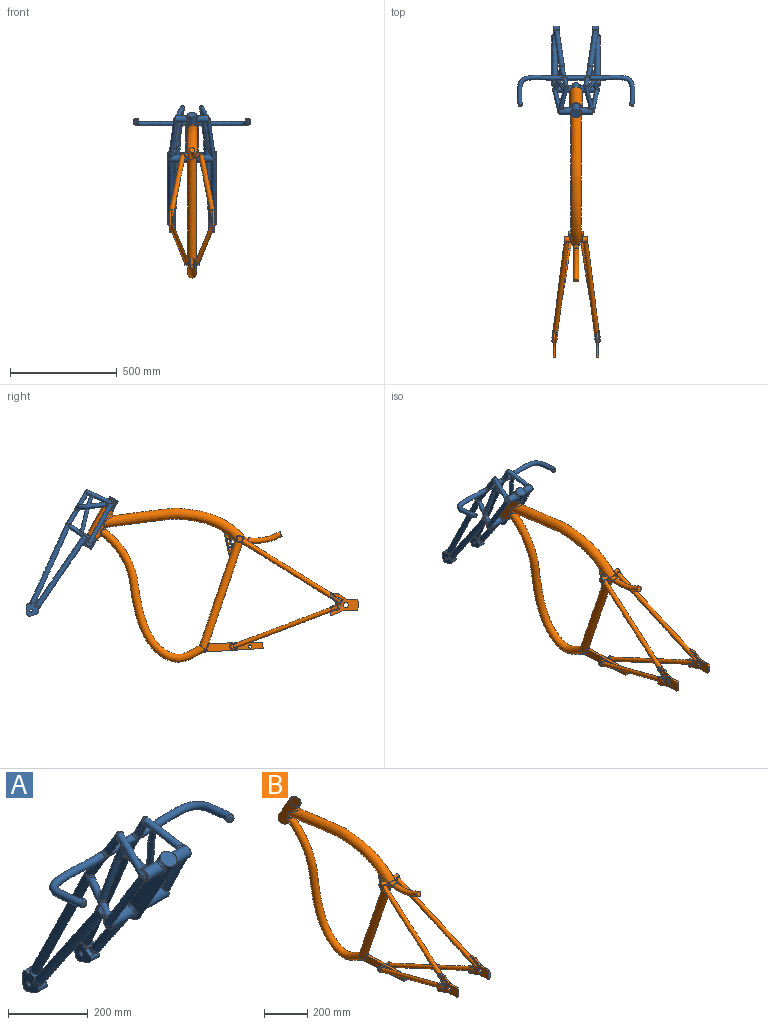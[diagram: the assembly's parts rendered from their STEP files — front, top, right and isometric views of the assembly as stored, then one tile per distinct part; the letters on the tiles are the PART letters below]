
ASSEMBLY  parts=2 mates=1
PART A: 124 faces, bbox 553.6x434.4x597.8 mm
  f0: plane 24.39x8.77mm, normal (0.09,0.58,-0.81), area 177mm2, adj f52,f55
  f1: cylinder r=12.5mm len=27.12mm, axis (-0.09,-0.58,0.81), area 754.7mm2, adj f48,f49,f50,f51,f57,f110,f111,f112
  f2: cylinder r=12.5mm len=27.12mm, axis (0.09,-0.58,0.81), area 754.7mm2, adj f35,f58,f59,f60,f63,f104,f105,f106
  f3: cylinder r=12.5mm len=25.53mm, axis (0.09,-0.58,0.81), area 364mm2, adj f61,f62,f63,f65,f101,f103
  f4: bspline ~89.4x61.57mm, area 4951.9mm2, adj f66,f90,f121,f122
  f5: bspline ~81.91x57.27mm, area 4325.2mm2, adj f79,f89,f120
  f6: bspline ~89.4x61.57mm, area 4951.7mm2, adj f56,f67,f114,f115
  f7: bspline ~81.91x57.27mm, area 4325.3mm2, adj f68,f70,f119
  f8: plane 3.04x1.93mm, normal (-0.24,-0.86,-0.46), area 3.5mm2, adj f30,f84,f88
  f9: plane 4.38x2.58mm, normal (0.24,-0.86,-0.46), area 1mm2, adj f39,f43
  f10: bspline ~109.3x81.16mm, area 5787.7mm2, adj f15,f23,f31,f35,f65,f66,f81,f90
  f11: cylinder r=16.33mm len=61.66mm, axis (1,0,0), area 4732.4mm2, adj f19,f39,f71,f76,f77,f94
  f12: plane 3.65x3.13mm, normal (1,0,0), area 1.5mm2, adj f39,f43,f77
  f13: cylinder r=16.33mm len=82.32mm, axis (1,0,0), area 7483.8mm2, adj f22,f36,f39,f40,f44,f92
  f14: plane 29.1x20.74mm, normal (-1,0,0), area 95.1mm2, adj f20,f82,f85,f86,f88
  f15: cylinder r=16.33mm len=82.32mm, axis (1,0,0), area 7485.1mm2, adj f10,f23,f26,f27,f31,f91
  f16: cylinder r=22.49mm len=247.36mm, axis (0,0.49,-0.87), area 30990.3mm2, adj f17,f18,f91,f92,f93,f94
  f17: plane 44.97x39.31mm, normal (0,-0.49,0.87), area 1588.4mm2, adj f16
  f18: plane 44.97x39.31mm, normal (0,0.49,-0.87), area 1588.4mm2, adj f16
  f19: plane 29.1x20.74mm, normal (1,0,0), area 95.1mm2, adj f11,f71,f72,f75,f76
  f20: cylinder r=16.33mm len=61.66mm, axis (1,0,0), area 4735.2mm2, adj f14,f26,f82,f83,f86,f93
  f21: plane 3.65x3.12mm, normal (-1,0,0), area 1.5mm2, adj f26,f30,f83
  f22: plane 32.69x28.52mm, normal (1,0,0), area 505.8mm2, adj f13,f36,f38,f39,f44
  f23: plane 32.69x28.52mm, normal (-1,0,0), area 505.8mm2, adj f10,f15,f25,f26,f31
  f24: plane 1.65x1.36mm, normal (0,-0.49,0.87), area 1mm2, adj f26,f84,f85
  f25: plane 17.48x10mm, normal (0,0.49,-0.87), area 157.1mm2, adj f23,f26
  f26: bspline ~197.67x121.81mm, area 12140mm2, adj f15,f20,f21,f23,f24,f25,f27,f28
  f27: plane 1.86x1.53mm, normal (-0.25,-0.76,-0.59), area 1.6mm2, adj f15,f26,f31
  f28: plane 4.38x2.58mm, normal (-0.24,-0.86,-0.46), area 1mm2, adj f26,f30
  f29: plane 11.6x8.61mm, normal (-0.25,-0.76,-0.59), area 27mm2, adj f26,f31
  f30: bspline ~130.96x72.65mm, area 6497mm2, adj f8,f21,f26,f28,f79,f80,f83,f84
  f31: bspline ~20.64x17.61mm, area 152.1mm2, adj f10,f15,f23,f26,f27,f29
  f32: bspline ~84.78x49.1mm, area 2363mm2, adj f33,f80
  f33: bspline ~140.91x45.51mm, area 6912.3mm2, adj f32,f81
  f34: plane 21.62x15.63mm, normal (0.09,-0.58,0.81), area 126.5mm2, adj f35,f118
  f35: bspline ~341.51x244.41mm, area 30533.3mm2, adj f2,f10,f34,f118
  f36: bspline ~109.3x81.16mm, area 5787.7mm2, adj f13,f22,f44,f48,f54,f56,f67,f78
  f37: plane 1.65x1.36mm, normal (0,-0.49,0.87), area 1mm2, adj f39,f72,f73
  f38: plane 17.48x10mm, normal (0,0.49,-0.87), area 157.1mm2, adj f22,f39
  f39: bspline ~197.67x121.81mm, area 12140mm2, adj f9,f11,f12,f13,f22,f37,f38,f40
  f40: plane 1.86x1.53mm, normal (0.25,-0.76,-0.59), area 1.6mm2, adj f13,f39,f44
  f41: plane 3.04x1.93mm, normal (0.24,-0.86,-0.46), area 3.5mm2, adj f43,f73,f75
  f42: plane 11.6x8.61mm, normal (0.25,-0.76,-0.59), area 27mm2, adj f39,f44
  f43: bspline ~130.96x72.65mm, area 6497mm2, adj f9,f12,f39,f41,f68,f69,f70,f73
  f44: bspline ~20.64x17.61mm, area 152.1mm2, adj f13,f22,f36,f39,f40,f42
  f45: bspline ~84.78x49.1mm, area 2363mm2, adj f46,f69
  f46: bspline ~140.91x45.51mm, area 6912.3mm2, adj f45,f78
  f47: plane 21.62x15.63mm, normal (-0.09,-0.58,0.81), area 126.5mm2, adj f48,f116
  f48: bspline ~341.51x244.41mm, area 30533.3mm2, adj f1,f36,f47,f116
  f49: extruded ~50.08x36.73mm, area 2051.5mm2, adj f1,f50,f52,f57,f110,f113
  f50: plane 65.89x61.72mm, normal (1,0,0), area 2550.6mm2, adj f1,f49,f51,f52,f53,f57
  f51: plane 29.55x17.87mm, normal (0,-0.52,0.85), area 212.1mm2, adj f1,f50,f52,f54,f55,f109,f112,f113
  f52: extruded ~61.93x29mm, area 2324.9mm2, adj f0,f49,f50,f51,f55,f108,f113
  f53: cylinder r=6.55mm len=29mm, axis (-1,0,0), area 1192.9mm2, adj f50,f113
  f54: bspline ~378.92x185.95mm, area 31091.1mm2, adj f36,f51,f55,f56,f107,f109
  f55: cylinder r=12.5mm len=25.53mm, axis (-0.09,-0.58,0.81), area 364mm2, adj f0,f51,f52,f54,f107,f108
  f56: plane 24.9x17.76mm, normal (-0.09,-0.58,0.81), area 113.5mm2, adj f6,f36,f54
  f57: plane 20.36x18.65mm, normal (0.09,0.58,-0.81), area 128.3mm2, adj f1,f49,f50
  f58: plane 20.36x18.65mm, normal (-0.09,0.58,-0.81), area 128.3mm2, adj f2,f59,f60
  f59: extruded ~50.08x36.73mm, area 2051.5mm2, adj f2,f58,f60,f62,f100,f106
  f60: plane 65.89x61.72mm, normal (-1,0,0), area 2550.6mm2, adj f2,f58,f59,f62,f63,f64
  f61: plane 24.39x8.77mm, normal (-0.09,0.58,-0.81), area 177mm2, adj f3,f62
  f62: extruded ~61.93x29mm, area 2324.9mm2, adj f3,f59,f60,f61,f63,f100,f101
  f63: plane 29.55x17.87mm, normal (0,-0.52,0.85), area 212.1mm2, adj f2,f3,f60,f62,f65,f100,f102,f105
  f64: cylinder r=6.55mm len=29mm, axis (1,0,0), area 1192.9mm2, adj f60,f100
  f65: bspline ~378.92x185.95mm, area 31091.1mm2, adj f3,f10,f63,f66,f102,f103
  f66: plane 24.9x17.76mm, normal (0.09,-0.58,0.81), area 113.5mm2, adj f4,f10,f65
  f67: bspline ~19.67x18.98mm, area 0mm2, adj f6,f36
  f68: bspline ~19.98x15.01mm, area 0mm2, adj f7,f43
  f69: bspline ~25.71x19.37mm, area 412.7mm2, adj f43,f45,f70
  f70: bspline ~20.39x19.79mm, area 187.8mm2, adj f7,f43,f69
  f71: bspline ~40.11x24.27mm, area 94.2mm2, adj f11,f19,f39,f72
  f72: cylinder r=6mm len=9.6mm, axis (0,-0.87,-0.49), area 39.6mm2, adj f19,f37,f39,f71,f74
  f73: cylinder r=6mm len=8.58mm, axis (-0.97,-0.21,-0.12), area 37.4mm2, adj f37,f39,f41,f43,f74
  f74: sphere r=6mm, area 47.4mm2, adj f72,f73,f75
  f75: cylinder r=6mm len=10.5mm, axis (0,0.47,-0.88), area 38.8mm2, adj f19,f41,f43,f74,f76
  f76: bspline ~35.25x16.64mm, area 131.8mm2, adj f11,f19,f43,f75,f77
  f77: bspline ~28.35x22.14mm, area 351mm2, adj f11,f12,f39,f43,f76
  f78: bspline ~25.05x23.15mm, area 437.1mm2, adj f36,f46
  f79: bspline ~20.39x19.79mm, area 187.8mm2, adj f5,f30,f80
  f80: bspline ~25.71x19.38mm, area 412.8mm2, adj f30,f32,f79
  f81: bspline ~25.05x23.15mm, area 437.1mm2, adj f10,f33
  f82: bspline ~37.76x23.12mm, area 94.1mm2, adj f14,f20,f26,f85
  f83: bspline ~28.35x22.14mm, area 351mm2, adj f20,f21,f26,f30,f86
  f84: cylinder r=6mm len=8.58mm, axis (0.97,-0.21,-0.12), area 37.4mm2, adj f8,f24,f26,f30,f87
  f85: cylinder r=6mm len=9.6mm, axis (0,0.87,0.49), area 39.6mm2, adj f14,f24,f26,f82,f87
  f86: bspline ~35.25x16.64mm, area 131.8mm2, adj f14,f20,f30,f83,f88
  f87: sphere r=6mm, area 35.8mm2, adj f84,f85,f88
  f88: cylinder r=6mm len=10.5mm, axis (0,-0.47,0.88), area 38.8mm2, adj f8,f14,f30,f86,f87
  f89: bspline ~19.98x15.01mm, area 0mm2, adj f5,f30
  f90: bspline ~19.67x18.98mm, area 0mm2, adj f4,f10
  f91: bspline ~42.66x37.71mm, area 790.4mm2, adj f15,f16
  f92: bspline ~42.64x37.7mm, area 790.6mm2, adj f13,f16
  f93: bspline ~42.66x37.71mm, area 790.3mm2, adj f16,f20
  f94: bspline ~42.66x37.7mm, area 790.9mm2, adj f11,f16
  f95: cylinder r=10.69mm len=138mm, axis (1,0,0), area 6988.7mm2, adj f97,f99,f114,f119,f120,f121
  f96: plane 11.33x10.58mm, normal (-0.36,-0.93,0.1), area 101.3mm2, adj f117
  f97: bspline ~206.22x143.31mm, area 20389.5mm2, adj f95,f115,f117
  f98: plane 11.34x10.59mm, normal (0.36,-0.93,0.1), area 101.3mm2, adj f123
  f99: bspline ~206.22x143.31mm, area 20389.5mm2, adj f95,f122,f123
  f100: plane 61.61x61.26mm, normal (1,0,0), area 2422mm2, adj f59,f62,f63,f64,f101,f102,f103,f104
  f101: plane 12.86x11.39mm, normal (0,-0.58,0.82), area 37.2mm2, adj f3,f62,f100,f103
  f102: extruded ~9.97x0.72mm, area 7.9mm2, adj f63,f65,f100,f103
  f103: extruded ~10.8x5.8mm, area 71.6mm2, adj f3,f65,f100,f101,f102
  f104: plane 15.67x15mm, normal (0,-0.58,0.82), area 227.8mm2, adj f2,f100,f105,f106
  f105: extruded ~15x9.08mm, area 159.8mm2, adj f2,f63,f100,f104
  f106: extruded ~15x0.62mm, area 12mm2, adj f2,f59,f100,f104
  f107: extruded ~10.8x5.8mm, area 71.6mm2, adj f54,f55,f108,f109,f113
  f108: plane 12.86x11.39mm, normal (0,-0.58,0.82), area 37.2mm2, adj f52,f55,f107,f113
  f109: extruded ~9.97x0.72mm, area 7.9mm2, adj f51,f54,f107,f113
  f110: extruded ~15x0.62mm, area 12mm2, adj f1,f49,f111,f113
  f111: plane 15.67x15mm, normal (0,-0.58,0.82), area 227.8mm2, adj f1,f110,f112,f113
  f112: extruded ~15x9.08mm, area 159.8mm2, adj f1,f51,f111,f113
  f113: plane 61.61x61.26mm, normal (-1,0,0), area 2422mm2, adj f49,f51,f52,f53,f107,f108,f109,f110
  f114: bspline ~27.27x19.55mm, area 281.1mm2, adj f6,f95,f115
  f115: bspline ~12.4x10.19mm, area 66.2mm2, adj f6,f97,f114
  f116: cylinder r=5mm len=22.71mm, axis (-0.25,0.8,0.54), area 147.6mm2, adj f36,f47,f48
  f117: bspline ~21.88x21.78mm, area 437.6mm2, adj f96,f97
  f118: cylinder r=5mm len=22.71mm, axis (0.25,0.8,0.54), area 147.6mm2, adj f10,f34,f35
  f119: bspline ~30.21x19.28mm, area 374.4mm2, adj f7,f95
  f120: bspline ~30.22x19.28mm, area 374.3mm2, adj f5,f95
  f121: bspline ~27.26x19.55mm, area 280.8mm2, adj f4,f95,f122
  f122: bspline ~12.5x10.39mm, area 66.2mm2, adj f4,f99,f121
  f123: bspline ~21.9x21.79mm, area 437.6mm2, adj f98,f99
PART B: 192 faces, bbox 230.8x1270.5x735.8 mm
  f0: bspline ~21.42x11.61mm, area 143.6mm2, adj f27,f165,f167,f168
  f1: bspline ~17.59x9.63mm, area 44.3mm2, adj f27,f164,f166,f171
  f2: bspline ~17.9x15.68mm, area 126mm2, adj f24,f171,f180,f184
  f3: bspline ~17.06x12.17mm, area 42.7mm2, adj f24,f167,f172,f173
  f4: plane 3.6x3.57mm, normal (-1,0,0), area 5.2mm2, adj f167,f174,f175
  f5: plane 28.04x21.48mm, normal (-1,0,0), area 263.4mm2, adj f167,f174,f181,f182
  f6: plane 6.88x5.58mm, normal (-1,0,0), area 14.1mm2, adj f174,f175,f182
  f7: plane 3.6x3.57mm, normal (1,0,0), area 5.2mm2, adj f171,f178,f179
  f8: plane 33.48x16.92mm, normal (1,0,0), area 255mm2, adj f170,f171,f178,f183
  f9: plane 6.88x5.58mm, normal (1,0,0), area 14.1mm2, adj f178,f179,f183
  f10: plane 4.96x2.3mm, normal (0,-0.45,-0.89), area 1.5mm2, adj f43,f151,f157
  f11: plane 132.93x37.64mm, normal (1,0,0), area 3689.4mm2, adj f29,f30,f31,f32,f137
  f12: plane 131.21x42.91mm, normal (-1,0,0), area 3945.4mm2, adj f29,f31,f110,f112,f113,f119
  f13: plane 14.26x5.68mm, normal (0,0.93,-0.35), area 13.8mm2, adj f14,f104,f114,f115
  f14: bspline ~493.81x203.46mm, area 31729.8mm2, adj f13,f15,f83,f101,f102,f114,f115,f116
  f15: plane 12.74x5.39mm, normal (0,1,0), area 9.9mm2, adj f14,f82,f99,f122,f125
  f16: plane 6.18x3.94mm, normal (-0.1,-0.84,-0.53), area 2.6mm2, adj f76,f131
  f17: plane 14.26x5.68mm, normal (0,0.93,-0.35), area 13.8mm2, adj f18,f73,f132,f133
  f18: bspline ~493.81x203.46mm, area 31729.8mm2, adj f17,f19,f64,f71,f72,f132,f133,f135
  f19: plane 14.81x13.34mm, normal (0,1,0), area 85.4mm2, adj f18,f63,f69,f70,f140,f143
  f20: plane 6.18x3.94mm, normal (0.1,-0.84,-0.53), area 2.6mm2, adj f46,f149
  f21: plane 16.94x10.55mm, normal (0,-0.45,-0.89), area 35.5mm2, adj f24,f27,f42,f152,f153
  f22: plane 16.94x10.55mm, normal (0,-0.45,-0.89), area 35.5mm2, adj f24,f27,f43,f150,f151
  f23: bspline ~628.58x495.84mm, area 101545mm2, adj f106,f108,f109,f110,f111,f155,f156
  f24: bspline ~656.99x154.64mm, area 101847.3mm2, adj f2,f3,f21,f22,f27,f151,f153,f154
  f25: plane 0.21x0mm, normal (0,-0.23,0.97), area 0mm2, adj f42,f152,f157
  f26: plane 0.21x0mm, normal (0,-0.23,0.97), area 0mm2, adj f43,f150,f157
  f27: bspline ~545.85x252.61mm, area 60746.3mm2, adj f0,f1,f21,f22,f24,f29,f36,f105
  f28: plane 4.97x2.3mm, normal (0,-0.45,-0.89), area 1.5mm2, adj f42,f153,f157
  f29: plane 256.89x20.13mm, normal (0,0.02,1), area 3223mm2, adj f11,f12,f27,f30,f33,f34,f105,f113
  f30: plane 29.33x12.7mm, normal (0,-1,0.05), area 372.8mm2, adj f11,f29,f31,f34
  f31: plane 279.37x17.58mm, normal (0,-0.06,-1), area 3534.2mm2, adj f11,f12,f30,f33,f34,f108,f109,f110
  f32: cylinder r=7.75mm len=15.51mm, axis (-1,0,0), area 618.8mm2, adj f11,f34
  f33: plane 131.21x42.91mm, normal (1,0,0), area 3945.4mm2, adj f29,f31,f105,f107,f108,f136
  f34: plane 132.93x37.64mm, normal (-1,0,0), area 3689.4mm2, adj f29,f30,f31,f32,f118
  f35: plane 28.93x26.96mm, normal (0,-0.92,0.39), area 506.7mm2, adj f36
  f36: bspline ~184.62x54.91mm, area 13445.3mm2, adj f27,f35,f157
  f37: plane 58.44x51.08mm, normal (0,-0.49,0.87), area 851.6mm2, adj f38,f40
  f38: cylinder r=29.22mm len=161.12mm, axis (0,0.49,-0.87), area 22591mm2, adj f37,f39,f154,f155
  f39: plane 58.44x51.08mm, normal (0,0.49,-0.87), area 851.6mm2, adj f38,f40
  f40: cylinder r=24.14mm len=156.19mm, axis (0,-0.49,0.87), area 23033.3mm2, adj f37,f39
  f41: plane 26.88x26.88mm, normal (1,0,0), area 506.7mm2, adj f42,f191
  f42: cylinder r=12.7mm len=39.18mm, axis (1,0,0), area 1803.5mm2, adj f21,f25,f28,f41,f152,f153,f157,f190
  f43: cylinder r=12.7mm len=39.18mm, axis (1,0,0), area 1802.3mm2, adj f10,f22,f26,f44,f150,f151,f157,f188
  f44: plane 26.88x26.88mm, normal (-1,0,0), area 506.7mm2, adj f43,f189
  f45: plane 12.62x8.29mm, normal (0.1,-0.84,-0.53), area 20.5mm2, adj f46,f47,f146
  f46: bspline ~482.12x311.22mm, area 37814.4mm2, adj f20,f45,f47,f48,f50,f51,f52,f144
  f47: bspline ~492.82x318.16mm, area 208.1mm2, adj f45,f46,f145,f146
  f48: plane 2.59x1.24mm, normal (0,1,0), area 0.5mm2, adj f46,f50,f144
  f49: plane 19.65x15.46mm, normal (0,0.62,-0.79), area 214mm2, adj f50,f68,f69,f147
  f50: cylinder r=12.08mm len=12.54mm, axis (-1,0,0), area 69.4mm2, adj f46,f48,f49,f69,f144,f147
  f51: plane 1.61x0.71mm, normal (0,1,0), area 0.2mm2, adj f46,f52,f145
  f52: plane 37.77x14.13mm, normal (0,0,1), area 240.4mm2, adj f46,f51,f53,f69,f70,f145,f148
  f53: cylinder r=8.03mm len=8.13mm, axis (-1,0,0), area 40.1mm2, adj f52,f54,f69,f70
  f54: plane 30.55x20.87mm, normal (0,-0.56,0.83), area 300.7mm2, adj f53,f55,f69,f70
  f55: cylinder r=11.7mm len=8.13mm, axis (-1,0,0), area 71.8mm2, adj f54,f56,f69,f70
  f56: plane 46.43x8.13mm, normal (0,0,1), area 377.4mm2, adj f55,f57,f69,f70
  f57: plane 10.86x8.13mm, normal (0,-0.92,0.38), area 95.5mm2, adj f56,f58,f69,f70
  f58: plane 29.49x8.13mm, normal (0,-1,0), area 239.7mm2, adj f57,f59,f69,f70
  f59: plane 10.5x8.13mm, normal (0,-0.93,-0.36), area 91.5mm2, adj f58,f60,f69,f70
  f60: plane 46.87x8.13mm, normal (0,0,-1), area 380.9mm2, adj f59,f61,f69,f70
  f61: cylinder r=47.47mm len=14.09mm, axis (-1,0,0), area 116.3mm2, adj f60,f62,f69,f70
  f62: plane 56.04x21.17mm, normal (0,-0.35,-0.94), area 486.9mm2, adj f61,f63,f69,f70
  f63: cylinder r=6.32mm len=9.34mm, axis (-1,0,0), area 106.3mm2, adj f19,f62,f69,f70
  f64: plane 12.76x5.41mm, normal (0,1,0), area 9.9mm2, adj f18,f65,f69,f139,f142
  f65: cylinder r=6.14mm len=10.18mm, axis (-1,0,0), area 89.1mm2, adj f64,f66,f69,f142
  f66: plane 17.56x8.16mm, normal (0,0.38,0.93), area 153.9mm2, adj f65,f68,f69,f70,f142
  f67: cylinder r=12.06mm len=24.13mm, axis (-1,0,0), area 616.1mm2, adj f69,f70
  f68: cylinder r=6.18mm len=11.22mm, axis (-1,0,0), area 114.4mm2, adj f49,f66,f69,f70,f147
  f69: plane 130.4x100.38mm, normal (1,0,0), area 5367.7mm2, adj f19,f49,f50,f52,f53,f54,f55,f56
  f70: plane 130.4x100.38mm, normal (-1,0,0), area 5021.1mm2, adj f19,f52,f53,f54,f55,f56,f57,f58
  f71: plane 22.2x9.07mm, normal (0,-0.93,0.35), area 56.7mm2, adj f18,f70,f142,f143
  f72: plane 11x4.62mm, normal (0,-0.93,0.35), area 12mm2, adj f18,f141
  f73: plane 24.79x23.39mm, normal (1,0,0), area 289.5mm2, adj f17,f74,f132,f133,f135
  f74: cylinder r=12.39mm len=24.77mm, axis (1,0,0), area 1159.1mm2, adj f73,f134,f135,f136,f137,f138
  f75: plane 12.62x8.29mm, normal (-0.1,-0.84,-0.53), area 20.5mm2, adj f76,f77,f128
  f76: bspline ~482.12x311.22mm, area 37814.3mm2, adj f16,f75,f77,f78,f95,f96,f98,f127
  f77: bspline ~492.82x318.16mm, area 208.1mm2, adj f75,f76,f126,f128
  f78: plane 2.59x1.24mm, normal (0,1,0), area 0.5mm2, adj f76,f98,f127
  f79: plane 19.65x15.46mm, normal (0,0.62,-0.79), area 214mm2, adj f80,f98,f99,f130
  f80: cylinder r=6.18mm len=11.22mm, axis (1,0,0), area 114.4mm2, adj f79,f81,f99,f100,f130
  f81: plane 17.56x8.15mm, normal (0,0.38,0.93), area 153.9mm2, adj f80,f82,f99,f100,f125
  f82: cylinder r=6.14mm len=10.18mm, axis (1,0,0), area 89.1mm2, adj f15,f81,f99,f125
  f83: plane 14.82x13.35mm, normal (0,1,0), area 85.4mm2, adj f14,f84,f99,f100,f121,f124
  f84: cylinder r=6.32mm len=9.34mm, axis (1,0,0), area 106.3mm2, adj f83,f85,f99,f100
  f85: plane 56.04x21.17mm, normal (0,-0.35,-0.94), area 486.9mm2, adj f84,f86,f99,f100
  f86: cylinder r=47.47mm len=14.09mm, axis (1,0,0), area 116.3mm2, adj f85,f87,f99,f100
  f87: plane 46.87x8.13mm, normal (0,0,-1), area 380.9mm2, adj f86,f88,f99,f100
  f88: plane 10.5x8.13mm, normal (0,-0.93,-0.36), area 91.5mm2, adj f87,f89,f99,f100
  f89: plane 29.49x8.13mm, normal (0,-1,0), area 239.7mm2, adj f88,f90,f99,f100
  f90: plane 10.86x8.13mm, normal (0,-0.92,0.38), area 95.5mm2, adj f89,f91,f99,f100
  f91: plane 46.43x8.13mm, normal (0,0,1), area 377.4mm2, adj f90,f92,f99,f100
  f92: cylinder r=11.7mm len=8.13mm, axis (1,0,0), area 71.8mm2, adj f91,f93,f99,f100
  f93: plane 30.55x20.87mm, normal (0,-0.56,0.83), area 300.7mm2, adj f92,f94,f99,f100
  f94: cylinder r=8.03mm len=8.13mm, axis (1,0,0), area 40.1mm2, adj f93,f95,f99,f100
  f95: plane 37.73x14.09mm, normal (0,0,1), area 240.4mm2, adj f76,f94,f96,f99,f100,f126,f129
  f96: plane 1.61x0.71mm, normal (0,1,0), area 0.2mm2, adj f76,f95,f126
  f97: cylinder r=12.06mm len=24.13mm, axis (1,0,0), area 616.1mm2, adj f99,f100
  f98: cylinder r=12.08mm len=12.54mm, axis (1,0,0), area 69.4mm2, adj f76,f78,f79,f99,f127,f130
  f99: plane 130.4x100.38mm, normal (-1,0,0), area 5367.7mm2, adj f15,f79,f80,f81,f82,f83,f84,f85
  f100: plane 130.4x100.38mm, normal (1,0,0), area 5021.1mm2, adj f80,f81,f83,f84,f85,f86,f87,f88
  f101: plane 22.2x9.07mm, normal (0,-0.93,0.35), area 56.7mm2, adj f14,f100,f124,f125
  f102: plane 11x4.62mm, normal (0,-0.93,0.35), area 12mm2, adj f14,f123
  f103: cylinder r=12.39mm len=24.77mm, axis (-1,0,0), area 1159.1mm2, adj f104,f116,f117,f118,f119,f120
  f104: plane 24.8x23.39mm, normal (-1,0,0), area 289.5mm2, adj f13,f103,f114,f115,f116
  f105: cylinder r=6mm len=33.44mm, axis (0,-0.32,0.95), area 206.6mm2, adj f27,f29,f33,f107
  f106: bspline ~14.59x12.57mm, area 28.3mm2, adj f23,f27,f107
  f107: bspline ~9.22x8.89mm, area 34.9mm2, adj f33,f105,f106,f108
  f108: bspline ~31.49x21.1mm, area 78.1mm2, adj f23,f31,f33,f107,f109
  f109: bspline ~26.84x11.09mm, area 62.9mm2, adj f23,f31,f108,f110
  f110: bspline ~31.49x21.1mm, area 78.1mm2, adj f12,f23,f31,f109,f112
  f111: bspline ~14.96x12.88mm, area 28.3mm2, adj f23,f27,f112
  f112: bspline ~9.3x8.79mm, area 34.9mm2, adj f12,f110,f111,f113
  f113: cylinder r=6mm len=33.44mm, axis (0,-0.32,0.95), area 206.6mm2, adj f12,f27,f29,f112
  f114: bspline ~19.77x6.98mm, area 43mm2, adj f13,f14,f104,f116
  f115: bspline ~18.25x12.67mm, area 43mm2, adj f13,f14,f104,f116
  f116: bspline ~29.05x20.81mm, area 285.2mm2, adj f14,f103,f104,f114,f115,f118
  f117: bspline ~17.39x6.72mm, area 100.7mm2, adj f29,f103,f118,f119
  f118: torus R=18.39mm, axis (1,0,0), area 334.7mm2, adj f34,f103,f116,f117,f120
  f119: torus R=18.39mm, axis (1,0,0), area 348mm2, adj f12,f103,f117,f120
  f120: bspline ~7.83x6.26mm, area 56.8mm2, adj f31,f103,f118,f119
  f121: bspline ~56.47x17.79mm, area 204.5mm2, adj f14,f83,f99,f123
  f122: bspline ~49.58x28.15mm, area 188.1mm2, adj f14,f15,f99,f123
  f123: cylinder r=6mm len=28.78mm, axis (0,-0.35,-0.93), area 187.3mm2, adj f14,f99,f102,f121,f122
  f124: bspline ~52.52x27.97mm, area 252.9mm2, adj f14,f83,f100,f101
  f125: bspline ~41.95x16.26mm, area 181.9mm2, adj f14,f15,f81,f82,f100,f101
  f126: bspline ~73.35x38.26mm, area 284.5mm2, adj f77,f95,f96,f99,f128
  f127: bspline ~63.28x49.16mm, area 267.1mm2, adj f76,f78,f98,f99,f128
  f128: cylinder r=6mm len=28.33mm, axis (0,-0.53,0.85), area 190.5mm2, adj f75,f76,f77,f99,f126,f127
  f129: bspline ~75.81x53.79mm, area 359.9mm2, adj f76,f95,f100,f131
  f130: bspline ~70.61x42.77mm, area 289.7mm2, adj f76,f79,f80,f98,f100,f131
  f131: cylinder r=6mm len=26.34mm, axis (0,0.53,-0.85), area 184.5mm2, adj f16,f76,f100,f129,f130
  f132: bspline ~18.74x12.97mm, area 43mm2, adj f17,f18,f73,f135
  f133: bspline ~20.74x7.3mm, area 43mm2, adj f17,f18,f73,f135
  f134: bspline ~17.39x6.72mm, area 100.7mm2, adj f29,f74,f136,f137
  f135: bspline ~28.57x20.81mm, area 285.2mm2, adj f18,f73,f74,f132,f133,f137
  f136: torus R=18.39mm, axis (1,0,0), area 348mm2, adj f33,f74,f134,f138
  f137: torus R=18.39mm, axis (1,0,0), area 334.7mm2, adj f11,f74,f134,f135,f138
  f138: bspline ~7.83x6.26mm, area 56.8mm2, adj f31,f74,f136,f137
  f139: bspline ~47.48x27.19mm, area 188.1mm2, adj f18,f64,f69,f141
  f140: bspline ~54.25x17.43mm, area 204.5mm2, adj f18,f19,f69,f141
  f141: cylinder r=6mm len=28.78mm, axis (0,0.35,0.93), area 187.3mm2, adj f18,f69,f72,f139,f140
  f142: bspline ~42.33x16.31mm, area 181.9mm2, adj f18,f64,f65,f66,f70,f71
  f143: bspline ~47.66x25.82mm, area 252.9mm2, adj f18,f19,f70,f71
  f144: bspline ~60.77x47.61mm, area 267.1mm2, adj f46,f48,f50,f69,f146
  f145: bspline ~75.93x39.55mm, area 284.5mm2, adj f47,f51,f52,f69,f146
  f146: cylinder r=6mm len=28.33mm, axis (0,0.53,-0.85), area 190.5mm2, adj f45,f46,f47,f69,f144,f145
  f147: bspline ~70.35x42.47mm, area 289.7mm2, adj f46,f49,f50,f68,f70,f149
  f148: bspline ~67.62x48.52mm, area 359.8mm2, adj f46,f52,f70,f149
  f149: cylinder r=6mm len=26.34mm, axis (0,-0.53,0.85), area 184.5mm2, adj f20,f46,f70,f147,f148
  f150: bspline ~28.87x17.74mm, area 254.2mm2, adj f22,f26,f27,f43,f157
  f151: bspline ~31.3x24.29mm, area 341.2mm2, adj f10,f22,f24,f43
  f152: bspline ~28.76x16.53mm, area 254.2mm2, adj f21,f25,f27,f42,f157
  f153: bspline ~31.05x24.39mm, area 341.3mm2, adj f21,f24,f28,f42
  f154: bspline ~68.08x52.11mm, area 1276.9mm2, adj f24,f38,f155
  f155: bspline ~44.2x41.6mm, area 914.8mm2, adj f23,f38,f154
  f156: bspline ~38.1x17.64mm, area 0mm2, adj f23,f27
  f157: bspline ~50.79x45.31mm, area 1329mm2, adj f10,f24,f25,f26,f27,f28,f36,f42
  f158: plane 11.4x2.47mm, normal (0,-0.98,0.21), area 23.2mm2, adj f164,f167,f171,f172
  f159: cylinder r=6.5mm len=13mm, axis (-1,0,0), area 81.7mm2, adj f174,f179
  f160: cylinder r=6.5mm len=13mm, axis (-1,0,0), area 81.7mm2, adj f175,f178
  f161: plane 113.61x24.61mm, normal (0,0.98,-0.21), area 232.4mm2, adj f169,f182,f183,f187
  f162: plane 28.04x21.48mm, normal (1,0,0), area 263.4mm2, adj f171,f179,f183,f184
  f163: plane 33.48x16.92mm, normal (-1,0,0), area 255mm2, adj f167,f168,f175,f182
  f164: bspline ~17.71x9.65mm, area 18.6mm2, adj f1,f27,f158,f165
  f165: bspline ~17.59x9.63mm, area 44.6mm2, adj f0,f27,f164,f167
  f166: bspline ~22.42x12.24mm, area 143.9mm2, adj f1,f27,f170,f171
  f167: cylinder r=5mm len=51.23mm, axis (0,-0.21,-0.98), area 169.8mm2, adj f0,f3,f4,f5,f158,f163,f165,f173
  f168: cylinder r=5mm len=31.18mm, axis (0,-0.32,0.95), area 172.3mm2, adj f0,f27,f163,f176
  f169: bspline ~4.42x3.06mm, area 4.8mm2, adj f27,f161,f176,f177
  f170: cylinder r=5mm len=31.18mm, axis (0,-0.32,0.95), area 172.3mm2, adj f8,f27,f166,f177
  f171: cylinder r=5mm len=51.23mm, axis (0,0.21,0.98), area 169.8mm2, adj f1,f2,f7,f8,f158,f162,f166,f178
  f172: bspline ~17.13x12.19mm, area 20.2mm2, adj f3,f24,f158,f180
  f173: bspline ~18x15.77mm, area 126.1mm2, adj f3,f24,f167,f181
  f174: torus R=11.5mm, axis (1,0,0), area 364.9mm2, adj f4,f5,f6,f159,f167,f175,f182
  f175: torus R=11.5mm, axis (1,0,0), area 364.9mm2, adj f4,f6,f160,f163,f167,f174,f182
  f176: bspline ~19.33x8.81mm, area 62.4mm2, adj f27,f168,f169,f182
  f177: bspline ~16.29x9.38mm, area 62.3mm2, adj f27,f169,f170,f183
  f178: torus R=11.5mm, axis (1,0,0), area 364.9mm2, adj f7,f8,f9,f160,f171,f179,f183
  f179: torus R=11.5mm, axis (1,0,0), area 364.9mm2, adj f7,f9,f159,f162,f171,f178,f183
  f180: bspline ~17.06x12.17mm, area 42.7mm2, adj f2,f24,f171,f172
  f181: bspline ~29.68x24.25mm, area 151.5mm2, adj f5,f24,f173,f185
  f182: cylinder r=5mm len=114.66mm, axis (0,0.21,0.98), area 813.1mm2, adj f5,f6,f161,f163,f174,f175,f176,f185
  f183: cylinder r=5mm len=114.66mm, axis (0,-0.21,-0.98), area 813.1mm2, adj f8,f9,f161,f162,f177,f178,f179,f186
  f184: bspline ~29.68x24.25mm, area 151.5mm2, adj f2,f24,f162,f186
  f185: bspline ~12.6x10.33mm, area 62.8mm2, adj f24,f181,f182,f187
  f186: bspline ~13.41x10.99mm, area 62.8mm2, adj f24,f183,f184,f187
  f187: bspline ~4.81x3.29mm, area 7.3mm2, adj f24,f161,f185,f186
  f188: bspline ~29.19x21.93mm, area 287.8mm2, adj f43,f76,f189
  f189: bspline ~17.43x13.04mm, area 54.1mm2, adj f44,f76,f188
  f190: bspline ~28.81x21.93mm, area 287.7mm2, adj f42,f46,f191
  f191: bspline ~16.97x13.18mm, area 54.1mm2, adj f41,f46,f190
PLACE A rot(axis=(0,-0.49,0.87),0deg) t=(-657.39,707.11,-463.63)mm
PLACE B t=(-657.38,707.11,-463.63)mm fixed
MATE revolute A.f16 <-> B.f38  axis (0,0.49,-0.87) through (-657.38,467.04,-65.94)mm
